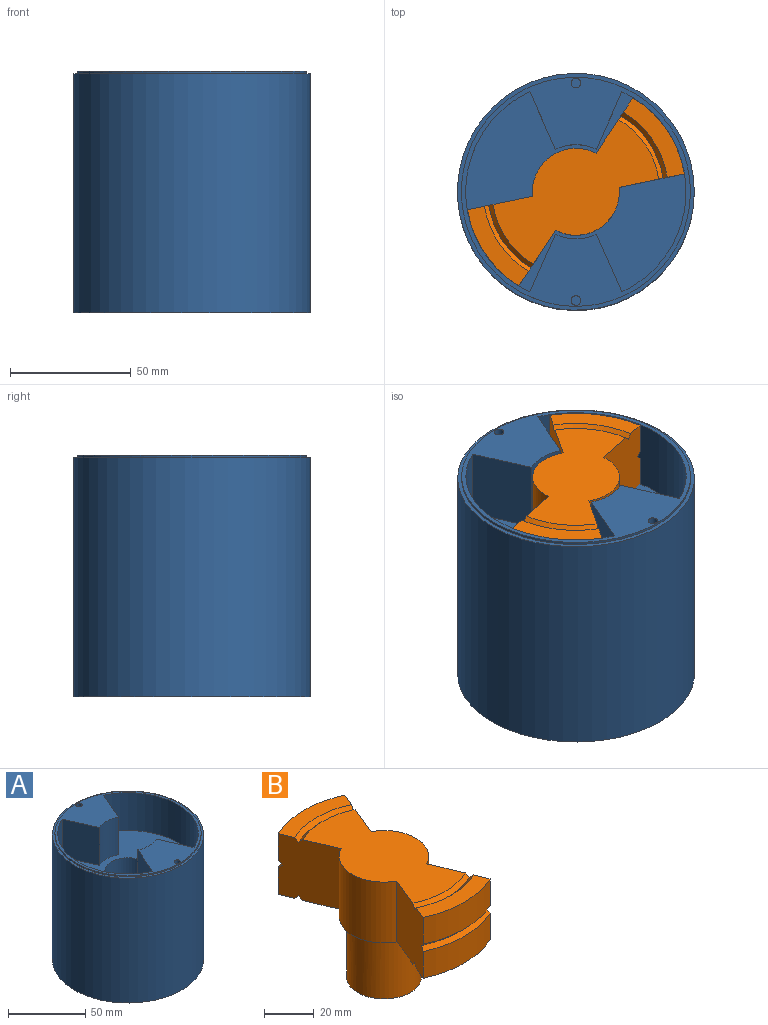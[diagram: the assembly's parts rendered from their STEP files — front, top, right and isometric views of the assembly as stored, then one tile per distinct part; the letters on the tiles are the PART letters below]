
ASSEMBLY  parts=2 mates=1
PART A: 27 faces, bbox 98x98x100 mm
  f0: cylinder r=49mm len=99mm, axis (0,0,1), area 30479.7mm2, adj f1,f3
  f1: plane 98x98mm, normal (0,0,-1), area 6958.4mm2, adj f0,f20,f21,f22,f23,f24,f25
  f2: cylinder r=47.4mm len=94.8mm, axis (0,0,1), area 297.8mm2, adj f3,f4
  f3: plane 98x98mm, normal (0,0,1), area 484.6mm2, adj f0,f2
  f4: plane 94.8x94.8mm, normal (0,0,1), area 1982.9mm2, adj f2,f5,f6,f7,f8,f9,f10,f11
  f5: cylinder r=19.5mm len=30mm, axis (0,0,1), area 527.7mm2, adj f4,f6,f12,f13
  f6: plane 30x23.9mm, normal (0.92,0.4,0), area 783.2mm2, adj f4,f5,f7,f13
  f7: cylinder r=45.6mm len=82.91mm, axis (0,0,1), area 3121.8mm2, adj f4,f6,f8,f13
  f8: plane 30x23.9mm, normal (0.92,-0.4,0), area 783.2mm2, adj f4,f7,f9,f13
  f9: cylinder r=19.5mm len=30mm, axis (0,0,1), area 527.7mm2, adj f4,f8,f10,f13
  f10: plane 30x23.9mm, normal (-0.92,-0.4,0), area 783.2mm2, adj f4,f9,f11,f13
  f11: cylinder r=45.6mm len=82.91mm, axis (0,0,1), area 3121.8mm2, adj f4,f10,f12,f13
  f12: plane 30x23.9mm, normal (-0.92,0.4,0), area 783.2mm2, adj f4,f5,f11,f13
  f13: plane 91.2x82.91mm, normal (0,0,1), area 4343.5mm2, adj f5,f6,f7,f8,f9,f10,f11,f12
  f14: cylinder r=15mm len=30mm, axis (0,0,1), area 2827.4mm2, adj f13,f15
  f15: plane 30x30mm, normal (0,0,1), area 706.9mm2, adj f14
  f16: cylinder r=2mm len=10mm, axis (0,0,1), area 125.7mm2, adj f4,f17
  f17: plane 4x4mm, normal (0,0,1), area 12.6mm2, adj f16
  f18: cylinder r=2mm len=10mm, axis (0,0,1), area 125.7mm2, adj f4,f19
  f19: plane 4x4mm, normal (0,0,1), area 12.6mm2, adj f18
  f20: plane 30x15mm, normal (-0.02,1,0), area 450mm2, adj f1,f21,f25,f26
  f21: plane 30x12.87mm, normal (0.86,0.51,0), area 450mm2, adj f1,f20,f22,f26
  f22: plane 30x13.11mm, normal (0.87,-0.49,0), area 450mm2, adj f1,f21,f23,f26
  f23: plane 30x15mm, normal (0.02,-1,0), area 450mm2, adj f1,f22,f24,f26
  f24: plane 30x12.87mm, normal (-0.86,-0.51,0), area 450mm2, adj f1,f23,f25,f26
  f25: plane 30x13.11mm, normal (-0.87,0.49,0), area 450mm2, adj f1,f20,f24,f26
  f26: plane 30x26.22mm, normal (0,0,-1), area 584.6mm2, adj f20,f21,f22,f23,f24,f25
PART B: 30 faces, bbox 38.1x91x59.7 mm
  f0: cylinder r=18mm len=31.73mm, axis (0,0,-1), area 1165.3mm2, adj f3,f6,f14,f18
  f1: cylinder r=18mm len=31.73mm, axis (0,0,-1), area 1165.3mm2, adj f2,f6,f14,f19
  f2: plane 30x25.48mm, normal (0.92,0.38,0), area 816.9mm2, adj f1,f6,f7,f8,f9,f10,f11,f12
  f3: plane 30x25.48mm, normal (-0.92,-0.38,0), area 816.9mm2, adj f0,f6,f14,f20,f21,f22,f23,f24
  f4: cylinder r=15mm len=30mm, axis (0,0,1), area 2799.2mm2, adj f5,f6
  f5: plane 30x30mm, normal (0,0,-1), area 706.9mm2, adj f4
  f6: plane 69.4x36mm, normal (0,0,-1), area 1120.3mm2, adj f0,f1,f2,f3,f4,f17,f18,f19
  f7: cylinder r=45.5mm len=38mm, axis (0,0,-1), area 517.5mm2, adj f2,f8,f16,f18
  f8: cone r=43.7mm half-angle=45deg, axis (0,0,-1), area 98mm2, adj f2,f7,f9,f18
  f9: cone r=45.5mm half-angle=45deg, axis (0,0,1), area 98mm2, adj f2,f8,f10,f18
  f10: cylinder r=45.5mm len=38mm, axis (0,0,-1), area 517.5mm2, adj f2,f9,f11,f18
  f11: plane 38x10.82mm, normal (0,0,1), area 262mm2, adj f2,f10,f12,f18
  f12: cone r=38.3mm half-angle=45deg, axis (0,0,1), area 83.7mm2, adj f2,f11,f13,f18
  f13: cone r=36.5mm half-angle=45deg, axis (0,0,-1), area 80.1mm2, adj f2,f12,f14,f18
  f14: plane 69.4x36mm, normal (0,0,1), area 1827.2mm2, adj f0,f1,f2,f3,f13,f18,f19,f27
  f15: cone r=38.3mm half-angle=45deg, axis (0,0,-1), area 83.7mm2, adj f2,f16,f17,f18
  f16: plane 38x10.82mm, normal (0,0,-1), area 262mm2, adj f2,f7,f15,f18
  f17: cone r=36.5mm half-angle=45deg, axis (0,0,1), area 80.1mm2, adj f2,f6,f15,f18
  f18: plane 30x25.48mm, normal (-0.92,0.38,0), area 816.9mm2, adj f0,f6,f7,f8,f9,f10,f11,f12
  f19: plane 30x25.48mm, normal (0.92,-0.38,0), area 816.9mm2, adj f1,f6,f14,f20,f21,f22,f23,f24
  f20: cylinder r=45.5mm len=38mm, axis (0,0,-1), area 517.5mm2, adj f3,f19,f21,f25
  f21: plane 38x10.82mm, normal (0,0,1), area 262mm2, adj f3,f19,f20,f26
  f22: plane 38x10.82mm, normal (0,0,-1), area 262mm2, adj f3,f19,f23,f28
  f23: cylinder r=45.5mm len=38mm, axis (0,0,-1), area 517.5mm2, adj f3,f19,f22,f24
  f24: cone r=43.7mm half-angle=45deg, axis (0,0,-1), area 98mm2, adj f3,f19,f23,f25
  f25: cone r=45.5mm half-angle=45deg, axis (0,0,1), area 98mm2, adj f3,f19,f20,f24
  f26: cone r=38.3mm half-angle=45deg, axis (0,0,1), area 83.7mm2, adj f3,f19,f21,f27
  f27: cone r=36.5mm half-angle=45deg, axis (0,0,-1), area 80.1mm2, adj f3,f14,f19,f26
  f28: cone r=38.3mm half-angle=45deg, axis (0,0,-1), area 83.7mm2, adj f3,f19,f22,f29
  f29: cone r=36.5mm half-angle=45deg, axis (0,0,1), area 80.1mm2, adj f3,f6,f19,f28
PLACE A at identity fixed
PLACE B rot(axis=(0,0,1),124.1deg) t=(0,0,-30.3)mm
MATE cylindrical B.f4 <-> A.f14  axis (0,0,-1) through (0,0,-60)mm
